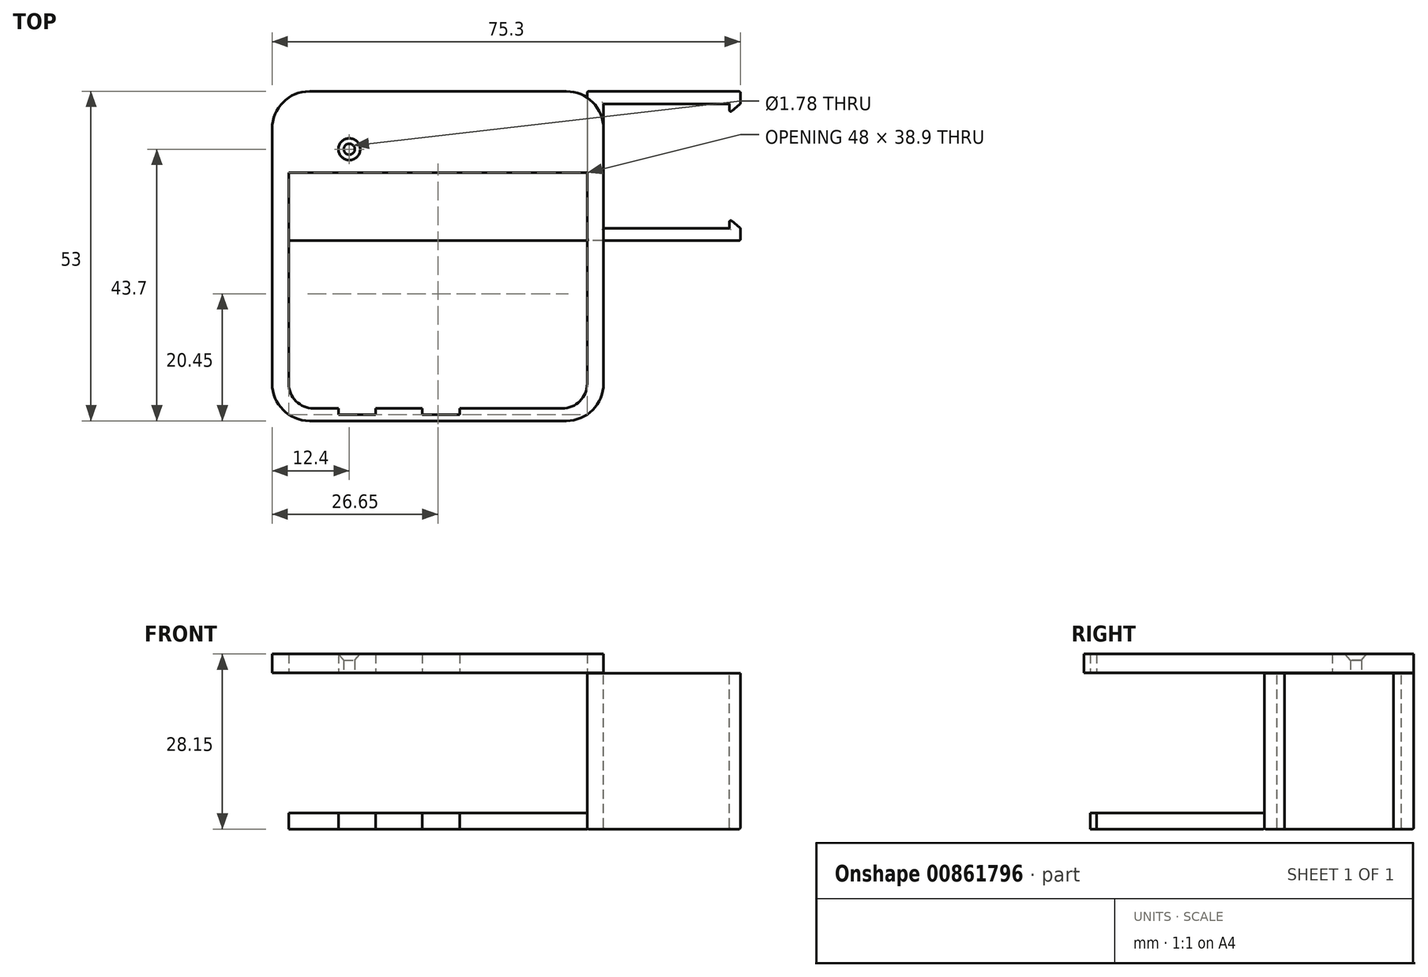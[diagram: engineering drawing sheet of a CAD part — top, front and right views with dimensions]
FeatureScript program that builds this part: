
annotation { "Feature Type Name" : "Feature", "Feature Type Description" : "" }
export const myFeature = defineFeature(function(context is Context, id is Id, definition is map)
    precondition{}
    {
        {
            var Q0;
            Q0=qCreatedBy(makeId("Top.planeOp"),FACE);
            var sketch = newSketch(context, id + "F0", { "sketchPlane" : qUnion([Q0])});
            skLineSegment(sketch, "E0.bottom", {"start": v(20.65, 26.5) * mm, "end": v(-20.65, 26.5) * mm});
            skLineSegment(sketch, "E0.top", {"start": v(20.65, -26.5) * mm, "end": v(-20.65, -26.5) * mm});
            skLineSegment(sketch, "E0.left", {"start": v(26.65, 20.5) * mm, "end": v(26.65, -20.5) * mm});
            skLineSegment(sketch, "E0.right", {"start": v(-26.65, 20.5) * mm, "end": v(-26.65, -20.5) * mm});
            skPoint(sketch, "E0.middle", {"position": v(0, 0) * mm});
            skPoint(sketch, "E1.visualSharp", {"position": v(-26.65, 26.5) * mm});
            skArc(sketch, "E1.filletArc", {"start": v(-20.65, 26.5) * mm, "mid": v(-24.9, 24.74) * mm, "end": v(-26.65, 20.5) * mm});
            skPoint(sketch, "E2.visualSharp", {"position": v(-26.65, -26.5) * mm});
            skArc(sketch, "E2.filletArc", {"start": v(-26.65, -20.5) * mm, "mid": v(-24.9, -24.74) * mm, "end": v(-20.65, -26.5) * mm});
            skPoint(sketch, "E3.visualSharp", {"position": v(26.65, -26.5) * mm});
            skArc(sketch, "E3.filletArc", {"start": v(20.65, -26.5) * mm, "mid": v(24.9, -24.74) * mm, "end": v(26.65, -20.5) * mm});
            skPoint(sketch, "E4.visualSharp", {"position": v(26.65, 26.5) * mm});
            skArc(sketch, "E4.filletArc", {"start": v(26.65, 20.5) * mm, "mid": v(24.9, 24.74) * mm, "end": v(20.65, 26.5) * mm});
            skSolve(sketch);
        }
        {
            var Q0;
            Q0=makeQuery(id+"F0.imprint","IMPRINT",FACE,{"disambiguationData":[TD([[makeQuery(id+"F0.imprint","IMPRINT",EDGE,{"derivedFrom":sQuery(id+"F0.wireOp",EDGE,"E0.bottom")}),1.0]])]});
            extrude(context, id + "F1", {"entities" : qUnion([Q0]), "depth" : (24.96 - 22.41) * mm, "offsetDistance" : 25 * mm});
        }
        {
            var Q0;
            Q0=makeQuery(id+"F1.opExtrude","CAP_FACE",FACE,{"disambiguationData":[OSD([sQuery(id+"F0.wireOp",EDGE,"E0.bottom"),sQuery(id+"F0.wireOp",EDGE,"E0.top"),sQuery(id+"F0.wireOp",EDGE,"E0.left"),sQuery(id+"F0.wireOp",EDGE,"E0.right"),sQuery(id+"F0.wireOp",EDGE,"E1.filletArc"),sQuery(id+"F0.wireOp",EDGE,"E2.filletArc"),sQuery(id+"F0.wireOp",EDGE,"E3.filletArc"),sQuery(id+"F0.wireOp",EDGE,"E4.filletArc")])],"isStart":false});
            var sketch = newSketch(context, id + "F2", { "sketchPlane" : qUnion([Q0])});
            skLineSegment(sketch, "E5.bottom", {"start": v(20, 24) * mm, "end": v(-20, 24) * mm});
            skLineSegment(sketch, "E5.top", {"start": v(20, -24) * mm, "end": v(-20, -24) * mm});
            skLineSegment(sketch, "E5.left", {"start": v(24, 20) * mm, "end": v(24, -20) * mm});
            skLineSegment(sketch, "E5.right", {"start": v(-24, 20) * mm, "end": v(-24, -20) * mm});
            skPoint(sketch, "E5.middle", {"position": v(0, 0) * mm});
            skPoint(sketch, "E6.visualSharp", {"position": v(-24, 24) * mm});
            skArc(sketch, "E6.filletArc", {"start": v(-20, 24) * mm, "mid": v(-22.83, 22.83) * mm, "end": v(-24, 20) * mm});
            skPoint(sketch, "E7.visualSharp", {"position": v(-24, -24) * mm});
            skArc(sketch, "E7.filletArc", {"start": v(-24, -20) * mm, "mid": v(-22.83, -22.83) * mm, "end": v(-20, -24) * mm});
            skPoint(sketch, "E8.visualSharp", {"position": v(24, -24) * mm});
            skArc(sketch, "E8.filletArc", {"start": v(20, -24) * mm, "mid": v(22.83, -22.83) * mm, "end": v(24, -20) * mm});
            skPoint(sketch, "E9.visualSharp", {"position": v(24, 24) * mm});
            skArc(sketch, "E9.filletArc", {"start": v(24, 20) * mm, "mid": v(22.83, 22.83) * mm, "end": v(20, 24) * mm});
            skSolve(sketch);
        }
        {
            var Q0;
            Q0=makeQuery(id+"F2.imprint","IMPRINT",FACE,{"disambiguationData":[TD([[makeQuery(id+"F2.imprint","IMPRINT",EDGE,{"derivedFrom":sQuery(id+"F2.wireOp",EDGE,"E5.bottom")}),-1.0]])]});
            extrude(context, id + "F3", {"entities" : qUnion([Q0]), "operationType" : NewBodyOperationType.ADD, "depth" : 22.5 * mm, "offsetDistance" : 25 * mm});
        }
        {
            var Q0;
            {var subQ0=sQuery(id+"F0.wireOp",EDGE,"E0.top");Q0=makeQuery(id+"F3.boolean.opBoolean","MERGE",FACE,{"derivedFrom":[makeQuery(id+"F1.opExtrude","SWEPT_FACE",FACE,{"disambiguationData":[OSD([subQ0])]}),makeQuery(id+"F3.opExtrude","SWEPT_FACE",FACE,{"disambiguationData":[OSD([subQ0])]})]});}
            var sketch = newSketch(context, id + "F4", { "sketchPlane" : qUnion([Q0])});
            skLineSegment(sketch, "E10.bottom", {"start": v(-15.5, 20.55) * mm, "end": v(-10.5, 20.55) * mm});
            skLineSegment(sketch, "E10.top", {"start": v(-15.5, 8.35) * mm, "end": v(-10.5, 8.35) * mm});
            skLineSegment(sketch, "E10.left", {"start": v(-15.5, 20.55) * mm, "end": v(-15.5, 8.35) * mm});
            skLineSegment(sketch, "E10.right", {"start": v(-10.5, 20.55) * mm, "end": v(-10.5, 8.35) * mm});
            skLineSegment(sketch, "E11.bottom", {"start": v(-2, 20.55) * mm, "end": v(3, 20.55) * mm});
            skLineSegment(sketch, "E11.top", {"start": v(-2, 8.35) * mm, "end": v(3, 8.35) * mm});
            skLineSegment(sketch, "E11.left", {"start": v(-2, 20.55) * mm, "end": v(-2, 8.35) * mm});
            skLineSegment(sketch, "E11.right", {"start": v(3, 20.55) * mm, "end": v(3, 8.35) * mm});
            skSolve(sketch);
        }
        {
            var Q0;
            Q0=makeQuery(id+"F4.imprint","IMPRINT",FACE,{"disambiguationData":[TD([[makeQuery(id+"F4.imprint","IMPRINT",EDGE,{"derivedFrom":sQuery(id+"F4.wireOp",EDGE,"E10.bottom")}),-1.0]])]});
            var Q1;
            Q1=makeQuery(id+"F4.imprint","IMPRINT",FACE,{"disambiguationData":[TD([[makeQuery(id+"F4.imprint","IMPRINT",EDGE,{"derivedFrom":sQuery(id+"F4.wireOp",EDGE,"E11.bottom")}),-1.0]])]});
            extrude(context, id + "F5", {"entities" : qUnion([Q0, Q1]), "operationType" : NewBodyOperationType.REMOVE, "oppositeDirection" : true, "depth" : 25 * mm, "offsetDistance" : 25 * mm});
        }
        {
            var Q0;
            Q0=makeQuery(id+"F1.opExtrude","CAP_FACE",FACE,{"disambiguationData":[OSD([sQuery(id+"F0.wireOp",EDGE,"E0.bottom"),sQuery(id+"F0.wireOp",EDGE,"E0.top"),sQuery(id+"F0.wireOp",EDGE,"E0.left"),sQuery(id+"F0.wireOp",EDGE,"E0.right"),sQuery(id+"F0.wireOp",EDGE,"E1.filletArc"),sQuery(id+"F0.wireOp",EDGE,"E2.filletArc"),sQuery(id+"F0.wireOp",EDGE,"E3.filletArc"),sQuery(id+"F0.wireOp",EDGE,"E4.filletArc")])],"isStart":false});
            var sketch = newSketch(context, id + "F6", { "sketchPlane" : qUnion([Q0])});
            skLineSegment(sketch, "E12.bottom", {"start": v(3, 24) * mm, "end": v(1.5, 24) * mm});
            skLineSegment(sketch, "E12.top", {"start": v(3, 11.7) * mm, "end": v(1.5, 11.7) * mm});
            skLineSegment(sketch, "E12.left", {"start": v(3, 24) * mm, "end": v(3, 11.7) * mm});
            skLineSegment(sketch, "E12.right", {"start": v(1.5, 24) * mm, "end": v(1.5, 11.7) * mm});
            skSolve(sketch);
        }
        {
            var Q0;
            Q0=makeQuery(id+"F6.imprint","IMPRINT",FACE,{"disambiguationData":[TD([[makeQuery(id+"F6.imprint","IMPRINT",EDGE,{"derivedFrom":sQuery(id+"F6.wireOp",EDGE,"E12.bottom")}),1.0]])]});
            var Q1;
            Q1=makeQuery(id+"F3.opExtrude","CAP_FACE",FACE,{"disambiguationData":[OSD([sQuery(id+"F0.wireOp",EDGE,"E0.bottom"),sQuery(id+"F0.wireOp",EDGE,"E0.top"),sQuery(id+"F0.wireOp",EDGE,"E0.left"),sQuery(id+"F0.wireOp",EDGE,"E0.right"),sQuery(id+"F0.wireOp",EDGE,"E1.filletArc"),sQuery(id+"F0.wireOp",EDGE,"E2.filletArc"),sQuery(id+"F0.wireOp",EDGE,"E3.filletArc"),sQuery(id+"F0.wireOp",EDGE,"E4.filletArc"),sQuery(id+"F2.wireOp",EDGE,"E5.bottom"),sQuery(id+"F2.wireOp",EDGE,"E5.top"),sQuery(id+"F2.wireOp",EDGE,"E5.left"),sQuery(id+"F2.wireOp",EDGE,"E5.right"),sQuery(id+"F2.wireOp",EDGE,"E6.filletArc"),sQuery(id+"F2.wireOp",EDGE,"E7.filletArc"),sQuery(id+"F2.wireOp",EDGE,"E8.filletArc"),sQuery(id+"F2.wireOp",EDGE,"E9.filletArc")])],"isStart":false});
            extrude(context, id + "F7", {"entities" : qUnion([Q0]), "operationType" : NewBodyOperationType.ADD, "endBound" : BoundingType.UP_TO_SURFACE, "depth" : 25 * mm, "endBoundEntityFace" : qUnion([Q1]), "offsetDistance" : 25 * mm});
        }
        {
            var Q0;
            Q0=makeQuery(id+"F7.opExtrude","CAP_EDGE",EDGE,{"disambiguationData":[OSD([sQuery(id+"F6.wireOp",EDGE,"E12.top")])],"isStart":false});
            chamfer(context, id + "F8", {"entities" : qUnion([Q0]), "chamferType" : ChamferType.TWO_OFFSETS, "width1" : 10 * mm, "oppositeDirection" : false, "width2" : 5 * mm, "tangentPropagation" : true});
        }
        {
            var Q0;
            {var subQ9=sQuery(id+"F2.wireOp",EDGE,"E9.filletArc");var subQ10=sQuery(id+"F2.wireOp",EDGE,"E5.bottom");Q0=makeQuery(id+"F7.boolean.opBoolean","SPLIT",FACE,{"disambiguationData":[TD([makeQuery(id+"F3.opExtrude","SWEPT_FACE",FACE,{"disambiguationData":[OSD([subQ9])]})])],"derivedFrom":makeQuery(id+"F3.opExtrude","SWEPT_FACE",FACE,{"disambiguationData":[OSD([subQ10])]})});}
            var sketch = newSketch(context, id + "F9", { "sketchPlane" : qUnion([Q0])});
            skLineSegment(sketch, "E13.bottom", {"start": v(14, 2.55) * mm, "end": v(4, 2.55) * mm});
            skLineSegment(sketch, "E13.top", {"start": v(14, 9.55) * mm, "end": v(4, 9.55) * mm});
            skLineSegment(sketch, "E13.left", {"start": v(14, 2.55) * mm, "end": v(14, 9.55) * mm});
            skLineSegment(sketch, "E13.right", {"start": v(4, 2.55) * mm, "end": v(4, 9.55) * mm});
            skSolve(sketch);
        }
        {
            var Q0;
            Q0=makeQuery(id+"F9.imprint","IMPRINT",FACE,{"disambiguationData":[TD([[makeQuery(id+"F9.imprint","IMPRINT",EDGE,{"derivedFrom":sQuery(id+"F9.wireOp",EDGE,"E13.bottom")}),-1.0]])]});
            extrude(context, id + "F10", {"entities" : qUnion([Q0]), "operationType" : NewBodyOperationType.REMOVE, "oppositeDirection" : true, "depth" : 25 * mm, "offsetDistance" : 25 * mm});
        }
        {
            var Q0;
            Q0=makeQuery(id+"F3.opExtrude","SWEPT_FACE",FACE,{"disambiguationData":[OSD([sQuery(id+"F2.wireOp",EDGE,"E5.top")])]});
            var sketch = newSketch(context, id + "F11", { "sketchPlane" : qUnion([Q0])});
            skLineSegment(sketch, "E14.bottom", {"start": v(-3, 20.55) * mm, "end": v(2, 20.55) * mm});
            skLineSegment(sketch, "E14.top", {"start": v(-3, 25.05) * mm, "end": v(2, 25.05) * mm});
            skLineSegment(sketch, "E14.left", {"start": v(-3, 20.55) * mm, "end": v(-3, 25.05) * mm});
            skLineSegment(sketch, "E14.right", {"start": v(2, 20.55) * mm, "end": v(2, 25.05) * mm});
            skLineSegment(sketch, "E15.bottom", {"start": v(10.5, 20.55) * mm, "end": v(15.5, 20.55) * mm});
            skLineSegment(sketch, "E15.top", {"start": v(10.5, 25.05) * mm, "end": v(15.5, 25.05) * mm});
            skLineSegment(sketch, "E15.left", {"start": v(10.5, 20.55) * mm, "end": v(10.5, 25.05) * mm});
            skLineSegment(sketch, "E15.right", {"start": v(15.5, 20.55) * mm, "end": v(15.5, 25.05) * mm});
            skSolve(sketch);
        }
        {
            var Q0;
            Q0=makeQuery(id+"F11.imprint","IMPRINT",FACE,{"disambiguationData":[TD([[makeQuery(id+"F11.imprint","IMPRINT",EDGE,{"derivedFrom":sQuery(id+"F11.wireOp",EDGE,"E14.bottom")}),-1.0]])]});
            var Q1;
            Q1=makeQuery(id+"F11.imprint","IMPRINT",FACE,{"disambiguationData":[TD([[makeQuery(id+"F11.imprint","IMPRINT",EDGE,{"derivedFrom":sQuery(id+"F11.wireOp",EDGE,"E15.bottom")}),-1.0]])]});
            extrude(context, id + "F12", {"entities" : qUnion([Q0, Q1]), "operationType" : NewBodyOperationType.REMOVE, "oppositeDirection" : true, "depth" : 1.5 * mm, "offsetDistance" : 25 * mm});
        }
        {
            var Q0;
            Q0=makeQuery(id+"F10.boolean.opBoolean","MERGE",FACE,{"derivedFrom":[makeQuery(id+"F1.opExtrude","CAP_FACE",FACE,{"disambiguationData":[OSD([sQuery(id+"F0.wireOp",EDGE,"E0.bottom"),sQuery(id+"F0.wireOp",EDGE,"E0.top"),sQuery(id+"F0.wireOp",EDGE,"E0.left"),sQuery(id+"F0.wireOp",EDGE,"E0.right"),sQuery(id+"F0.wireOp",EDGE,"E1.filletArc"),sQuery(id+"F0.wireOp",EDGE,"E2.filletArc"),sQuery(id+"F0.wireOp",EDGE,"E3.filletArc"),sQuery(id+"F0.wireOp",EDGE,"E4.filletArc")])],"isStart":false}),makeQuery(id+"F10.opExtrude","SWEPT_FACE",FACE,{"disambiguationData":[OSD([sQuery(id+"F9.wireOp",EDGE,"E13.bottom")])]})]});
            var sketch = newSketch(context, id + "F13", { "sketchPlane" : qUnion([Q0])});
            skCircle(sketch, "E16", {"center": v(-14.25, 17.2) * mm, "radius": 4.5 * mm});
            skSolve(sketch);
        }
        {
            var Q0;
            Q0=makeQuery(id+"F13.imprint","IMPRINT",FACE,{"disambiguationData":[TD([[makeQuery(id+"F13.imprint","IMPRINT",EDGE,{"derivedFrom":sQuery(id+"F13.wireOp",EDGE,"E16")}),1.0]])]});
            var Q1;
            Q1=makeQuery(id+"F7.boolean.opBoolean","MERGE",FACE,{"derivedFrom":[makeQuery(id+"F3.opExtrude","CAP_FACE",FACE,{"disambiguationData":[OSD([sQuery(id+"F0.wireOp",EDGE,"E0.bottom"),sQuery(id+"F0.wireOp",EDGE,"E0.top"),sQuery(id+"F0.wireOp",EDGE,"E0.left"),sQuery(id+"F0.wireOp",EDGE,"E0.right"),sQuery(id+"F0.wireOp",EDGE,"E1.filletArc"),sQuery(id+"F0.wireOp",EDGE,"E2.filletArc"),sQuery(id+"F0.wireOp",EDGE,"E3.filletArc"),sQuery(id+"F0.wireOp",EDGE,"E4.filletArc"),sQuery(id+"F2.wireOp",EDGE,"E5.bottom"),sQuery(id+"F2.wireOp",EDGE,"E5.top"),sQuery(id+"F2.wireOp",EDGE,"E5.left"),sQuery(id+"F2.wireOp",EDGE,"E5.right"),sQuery(id+"F2.wireOp",EDGE,"E6.filletArc"),sQuery(id+"F2.wireOp",EDGE,"E7.filletArc"),sQuery(id+"F2.wireOp",EDGE,"E8.filletArc"),sQuery(id+"F2.wireOp",EDGE,"E9.filletArc")])],"isStart":false}),makeQuery(id+"F7.opExtrude","CAP_FACE",FACE,{"disambiguationData":[OSD([sQuery(id+"F6.wireOp",EDGE,"E12.bottom"),sQuery(id+"F6.wireOp",EDGE,"E12.top"),sQuery(id+"F6.wireOp",EDGE,"E12.left"),sQuery(id+"F6.wireOp",EDGE,"E12.right")])],"isStart":false})]});
            extrude(context, id + "F14", {"entities" : qUnion([Q0]), "operationType" : NewBodyOperationType.ADD, "endBound" : BoundingType.UP_TO_SURFACE, "depth" : 25 * mm, "endBoundEntityFace" : qUnion([Q1]), "offsetDistance" : 25 * mm});
        }
        {
            var Q0;
            Q0=makeQuery(id+"F7.boolean.opBoolean","MERGE",FACE,{"derivedFrom":[makeQuery(id+"F3.opExtrude","CAP_FACE",FACE,{"disambiguationData":[OSD([sQuery(id+"F0.wireOp",EDGE,"E0.bottom"),sQuery(id+"F0.wireOp",EDGE,"E0.top"),sQuery(id+"F0.wireOp",EDGE,"E0.left"),sQuery(id+"F0.wireOp",EDGE,"E0.right"),sQuery(id+"F0.wireOp",EDGE,"E1.filletArc"),sQuery(id+"F0.wireOp",EDGE,"E2.filletArc"),sQuery(id+"F0.wireOp",EDGE,"E3.filletArc"),sQuery(id+"F0.wireOp",EDGE,"E4.filletArc"),sQuery(id+"F2.wireOp",EDGE,"E5.bottom"),sQuery(id+"F2.wireOp",EDGE,"E5.top"),sQuery(id+"F2.wireOp",EDGE,"E5.left"),sQuery(id+"F2.wireOp",EDGE,"E5.right"),sQuery(id+"F2.wireOp",EDGE,"E6.filletArc"),sQuery(id+"F2.wireOp",EDGE,"E7.filletArc"),sQuery(id+"F2.wireOp",EDGE,"E8.filletArc"),sQuery(id+"F2.wireOp",EDGE,"E9.filletArc")])],"isStart":false}),makeQuery(id+"F7.opExtrude","CAP_FACE",FACE,{"disambiguationData":[OSD([sQuery(id+"F6.wireOp",EDGE,"E12.bottom"),sQuery(id+"F6.wireOp",EDGE,"E12.top"),sQuery(id+"F6.wireOp",EDGE,"E12.left"),sQuery(id+"F6.wireOp",EDGE,"E12.right")])],"isStart":false})]});
            cPlane(context, id + "F15", {"entities" : qUnion([Q0]), "cplaneType" : CPlaneType.OFFSET, "offset" : .1 * mm, "width" : 150 * mm, "height" : 150 * mm});
        }
        {
            var Q0;
            Q0=qCreatedBy(id+"F15.planeOp",FACE);
            var sketch = newSketch(context, id + "F16", { "sketchPlane" : qUnion([Q0])});
            skLineSegment(sketch, "E17.0", {"start": v(20.65, 26.5) * mm, "end": v(-20.65, 26.5) * mm});
            skArc(sketch, "E18.0", {"start": v(-20.65, 26.5) * mm, "mid": v(-24.9, 24.74) * mm, "end": v(-26.65, 20.5) * mm});
            skLineSegment(sketch, "E19.0", {"start": v(-26.65, 20.5) * mm, "end": v(-26.65, -20.5) * mm});
            skArc(sketch, "E20.0", {"start": v(-26.65, -20.5) * mm, "mid": v(-24.9, -24.74) * mm, "end": v(-20.65, -26.5) * mm});
            skLineSegment(sketch, "E21.0", {"start": v(20.65, -26.5) * mm, "end": v(-20.65, -26.5) * mm});
            skArc(sketch, "E22.0", {"start": v(20.65, -26.5) * mm, "mid": v(24.9, -24.74) * mm, "end": v(26.65, -20.5) * mm});
            skLineSegment(sketch, "E23.0", {"start": v(26.65, 20.5) * mm, "end": v(26.65, -20.5) * mm});
            skArc(sketch, "E24.0", {"start": v(26.65, 20.5) * mm, "mid": v(24.9, 24.74) * mm, "end": v(20.65, 26.5) * mm});
            skSolve(sketch);
        }
        {
            var Q0;
            Q0=makeQuery(id+"F16.imprint","IMPRINT",FACE,{"disambiguationData":[TD([[makeQuery(id+"F16.imprint","IMPRINT",EDGE,{"derivedFrom":sQuery(id+"F16.wireOp",EDGE,"E17.0")}),1.0]])]});
            extrude(context, id + "F17", {"entities" : qUnion([Q0]), "depth" : 3 * mm, "offsetDistance" : 25 * mm});
        }
        {
            var Q0;
            Q0=makeQuery(id+"F17.opExtrude","CAP_FACE",FACE,{"disambiguationData":[OSD([sQuery(id+"F16.wireOp",EDGE,"E17.0"),sQuery(id+"F16.wireOp",EDGE,"E18.0"),sQuery(id+"F16.wireOp",EDGE,"E19.0"),sQuery(id+"F16.wireOp",EDGE,"E20.0"),sQuery(id+"F16.wireOp",EDGE,"E21.0"),sQuery(id+"F16.wireOp",EDGE,"E22.0"),sQuery(id+"F16.wireOp",EDGE,"E23.0"),sQuery(id+"F16.wireOp",EDGE,"E24.0")])],"isStart":false});
            var sketch = newSketch(context, id + "F18", { "sketchPlane" : qUnion([Q0])});
            skPoint(sketch, "E25", {"position": v(-14.25, 17.2) * mm});
            skSolve(sketch);
        }
        {
            var Q0;
            Q0=sQuery(id+"F18.wireOp",VERTEX,"E25");
            var Q1;
            Q1=makeQuery(id+"F1.opExtrude","SWEPT_BODY",BODY,{"disambiguationData":[OSD([sQuery(id+"F0.wireOp",EDGE,"E0.bottom"),sQuery(id+"F0.wireOp",EDGE,"E0.top"),sQuery(id+"F0.wireOp",EDGE,"E0.left"),sQuery(id+"F0.wireOp",EDGE,"E0.right"),sQuery(id+"F0.wireOp",EDGE,"E1.filletArc"),sQuery(id+"F0.wireOp",EDGE,"E2.filletArc"),sQuery(id+"F0.wireOp",EDGE,"E3.filletArc"),sQuery(id+"F0.wireOp",EDGE,"E4.filletArc")])]});
            var Q2;
            Q2=makeQuery(id+"F17.opExtrude","SWEPT_BODY",BODY,{"disambiguationData":[OSD([sQuery(id+"F16.wireOp",EDGE,"E17.0"),sQuery(id+"F16.wireOp",EDGE,"E18.0"),sQuery(id+"F16.wireOp",EDGE,"E19.0"),sQuery(id+"F16.wireOp",EDGE,"E20.0"),sQuery(id+"F16.wireOp",EDGE,"E21.0"),sQuery(id+"F16.wireOp",EDGE,"E22.0"),sQuery(id+"F16.wireOp",EDGE,"E23.0"),sQuery(id+"F16.wireOp",EDGE,"E24.0")])]});
            hole(context, id + "F19", {"style" : HoleStyle.C_SINK, "endStyle" : HoleEndStyle.BLIND, "standardTappedOrClearance" : lookupTablePath({ "fit" : "Normal (ASME)", "standard" : "ANSI", "size" : "#0", "type" : "Clearance" }), "standardBlindInLast" : lookupTablePath({ "fit" : "Free", "standard" : "ANSI", "size" : "#0", "type" : "Clearance" }), "holeDiameter" : 1.78 * mm, "cSinkDiameter" : 3.5 * mm, "cSinkAngle" : 82 * degree, "majorDiameter" : 5 * mm, "holeDepth" : 12 * mm, "isTappedThrough" : true, "tappedDepth" : 12 * mm, "tapClearance" : 3, "locations" : qUnion([Q0]), "scope" : qUnion([Q1, Q2]), "startStyle" : HoleStartStyle.PART});
        }
        {
            var Q0;
            {var subQ0=sQuery(id+"F0.wireOp",EDGE,"E0.left");Q0=makeQuery(id+"F3.boolean.opBoolean","MERGE",FACE,{"derivedFrom":[makeQuery(id+"F1.opExtrude","SWEPT_FACE",FACE,{"disambiguationData":[OSD([subQ0])]}),makeQuery(id+"F3.opExtrude","SWEPT_FACE",FACE,{"disambiguationData":[OSD([subQ0])]})]});}
            var sketch = newSketch(context, id + "F20", { "sketchPlane" : qUnion([Q0])});
            skLineSegment(sketch, "E26.bottom", {"start": v(4.5, 0) * mm, "end": v(2.5, 0) * mm});
            skLineSegment(sketch, "E26.top", {"start": v(4.5, 25.15) * mm, "end": v(2.5, 25.15) * mm});
            skLineSegment(sketch, "E26.left", {"start": v(4.5, 0) * mm, "end": v(4.5, 25.15) * mm});
            skLineSegment(sketch, "E26.right", {"start": v(2.5, 0) * mm, "end": v(2.5, 25.15) * mm});
            skLineSegment(sketch, "E27.bottom", {"start": v(26.5, 0) * mm, "end": v(24.5, 0) * mm});
            skLineSegment(sketch, "E27.top", {"start": v(26.5, 25.05) * mm, "end": v(24.5, 25.05) * mm});
            skLineSegment(sketch, "E27.left", {"start": v(26.5, 0) * mm, "end": v(26.5, 25.05) * mm});
            skLineSegment(sketch, "E27.right", {"start": v(24.5, 0) * mm, "end": v(24.5, 25.05) * mm});
            skSolve(sketch);
        }
        {
            var Q0;
            {var subQ0=sQuery(id+"F20.wireOp",EDGE,"E26.bottom");Q0=makeQuery(id+"F20.imprint","IMPRINT",FACE,{"disambiguationData":[TD([[makeQuery(id+"F20.imprint","IMPRINT",EDGE,{"derivedFrom":subQ0}),-1.0]])]});}
            var Q1;
            Q1=makeQuery(id+"F20.imprint","IMPRINT",FACE,{"disambiguationData":[TD([[makeQuery(id+"F20.imprint","IMPRINT",EDGE,{"derivedFrom":sQuery(id+"F20.wireOp",EDGE,"E27.bottom")}),-1.0]])]});
            var Q2;
            {var subQ0=sQuery(id+"F0.wireOp",EDGE,"E4.filletArc");Q2=makeQuery(id+"F3.boolean.opBoolean","MERGE",FACE,{"derivedFrom":[makeQuery(id+"F1.opExtrude","SWEPT_FACE",FACE,{"disambiguationData":[OSD([subQ0])]}),makeQuery(id+"F3.opExtrude","SWEPT_FACE",FACE,{"disambiguationData":[OSD([subQ0])]})]});}
            var Q3;
            Q3=makeQuery(id+"F1.opExtrude","SWEPT_BODY",BODY,{"disambiguationData":[OSD([sQuery(id+"F0.wireOp",EDGE,"E0.bottom"),sQuery(id+"F0.wireOp",EDGE,"E0.top"),sQuery(id+"F0.wireOp",EDGE,"E0.left"),sQuery(id+"F0.wireOp",EDGE,"E0.right"),sQuery(id+"F0.wireOp",EDGE,"E1.filletArc"),sQuery(id+"F0.wireOp",EDGE,"E2.filletArc"),sQuery(id+"F0.wireOp",EDGE,"E3.filletArc"),sQuery(id+"F0.wireOp",EDGE,"E4.filletArc")])]});
            extrude(context, id + "F21", {"entities" : qUnion([Q0, Q1]), "operationType" : NewBodyOperationType.ADD, "depth" : 22 * mm, "offsetDistance" : 25 * mm});
        }
        {
            var Q0;
            Q0=makeQuery(id+"F21.opExtrude","CAP_FACE",FACE,{"disambiguationData":[OSD([sQuery(id+"F20.wireOp",EDGE,"E27.bottom"),sQuery(id+"F20.wireOp",EDGE,"E27.top"),sQuery(id+"F20.wireOp",EDGE,"E27.left"),sQuery(id+"F20.wireOp",EDGE,"E27.right")])],"isStart":true});
            var sketch = newSketch(context, id + "F22", { "sketchPlane" : qUnion([Q0])});
            skLineSegment(sketch, "E28.0.0", {"start": v(-26.5, 25.05) * mm, "end": v(-26.5, 0) * mm});
            skLineSegment(sketch, "E28.0.1", {"start": v(-26.5, 0) * mm, "end": v(-24.5, 0) * mm});
            skLineSegment(sketch, "E28.0.2", {"start": v(-24.5, 0) * mm, "end": v(-24.5, 25.05) * mm});
            skLineSegment(sketch, "E28.0.3", {"start": v(-24.5, 25.05) * mm, "end": v(-26.5, 25.05) * mm});
            skSolve(sketch);
        }
        {
            var Q0;
            Q0=makeQuery(id+"F22.imprint","IMPRINT",FACE,{"disambiguationData":[TD([[makeQuery(id+"F22.imprint","IMPRINT",EDGE,{"derivedFrom":sQuery(id+"F22.wireOp",EDGE,"E28.0.0")}),-1.0]])]});
            extrude(context, id + "F23", {"entities" : qUnion([Q0]), "operationType" : NewBodyOperationType.ADD, "endBound" : BoundingType.UP_TO_NEXT, "depth" : 25 * mm, "offsetDistance" : 25 * mm});
        }
        {
            var Q0;
            {var subQ0=sQuery(id+"F0.wireOp",EDGE,"E0.left");Q0=makeQuery(id+"F23.boolean.opBoolean","MERGE",FACE,{"derivedFrom":[makeQuery(id+"F21.opExtrude","SWEPT_FACE",FACE,{"disambiguationData":[OSD([sQuery(id+"F20.wireOp",EDGE,"E27.top")])]}),makeQuery(id+"F21.boolean.opBoolean","MERGE",FACE,{"derivedFrom":[makeQuery(id+"F7.boolean.opBoolean","MERGE",FACE,{"derivedFrom":[makeQuery(id+"F3.opExtrude","CAP_FACE",FACE,{"disambiguationData":[OSD([sQuery(id+"F0.wireOp",EDGE,"E0.bottom"),sQuery(id+"F0.wireOp",EDGE,"E0.top"),subQ0,sQuery(id+"F0.wireOp",EDGE,"E0.right"),sQuery(id+"F0.wireOp",EDGE,"E1.filletArc"),sQuery(id+"F0.wireOp",EDGE,"E2.filletArc"),sQuery(id+"F0.wireOp",EDGE,"E3.filletArc"),sQuery(id+"F0.wireOp",EDGE,"E4.filletArc"),sQuery(id+"F2.wireOp",EDGE,"E5.bottom"),sQuery(id+"F2.wireOp",EDGE,"E5.top"),sQuery(id+"F2.wireOp",EDGE,"E5.left"),sQuery(id+"F2.wireOp",EDGE,"E5.right"),sQuery(id+"F2.wireOp",EDGE,"E6.filletArc"),sQuery(id+"F2.wireOp",EDGE,"E7.filletArc"),sQuery(id+"F2.wireOp",EDGE,"E8.filletArc"),sQuery(id+"F2.wireOp",EDGE,"E9.filletArc")])],"isStart":false}),makeQuery(id+"F7.opExtrude","CAP_FACE",FACE,{"disambiguationData":[OSD([sQuery(id+"F6.wireOp",EDGE,"E12.bottom"),sQuery(id+"F6.wireOp",EDGE,"E12.top"),sQuery(id+"F6.wireOp",EDGE,"E12.left"),sQuery(id+"F6.wireOp",EDGE,"E12.right")])],"isStart":false})]}),makeQuery(id+"F21.opExtrude","SWEPT_FACE",FACE,{"disambiguationData":[OSD([subQ0])]})]}),makeQuery(id+"F23.opExtrude","SWEPT_FACE",FACE,{"disambiguationData":[OSD([sQuery(id+"F22.wireOp",EDGE,"E28.0.3")])]})]});}
            var sketch = newSketch(context, id + "F24", { "sketchPlane" : qUnion([Q0])});
            skLineSegment(sketch, "E29", {"start": v(48.65, 24.5) * mm, "end": v(46.85, 23) * mm});
            skLineSegment(sketch, "E30", {"start": v(46.85, 23) * mm, "end": v(46.85, 24.5) * mm});
            skLineSegment(sketch, "E31", {"start": v(48.65, 4.5) * mm, "end": v(46.85, 6) * mm});
            skLineSegment(sketch, "E32", {"start": v(46.85, 6) * mm, "end": v(46.85, 4.5) * mm});
            skSolve(sketch);
        }
        {
            var Q0;
            {var subQ0=sQuery(id+"F24.wireOp",EDGE,"E29");Q0=makeQuery(id+"F24.imprint","IMPRINT",FACE,{"disambiguationData":[TD([[makeQuery(id+"F24.imprint","IMPRINT",EDGE,{"derivedFrom":subQ0}),-1.0]])]});}
            var Q1;
            {var subQ0=sQuery(id+"F24.wireOp",EDGE,"E31");Q1=makeQuery(id+"F24.imprint","IMPRINT",FACE,{"disambiguationData":[TD([[makeQuery(id+"F24.imprint","IMPRINT",EDGE,{"derivedFrom":subQ0}),1.0]])]});}
            var Q2;
            Q2=makeQuery(id+"F23.boolean.opBoolean","MERGE",FACE,{"derivedFrom":[makeQuery(id+"F21.opExtrude","SWEPT_FACE",FACE,{"disambiguationData":[OSD([sQuery(id+"F20.wireOp",EDGE,"E27.bottom")])]}),makeQuery(id+"F21.boolean.opBoolean","MERGE",FACE,{"derivedFrom":[makeQuery(id+"F1.opExtrude","CAP_FACE",FACE,{"disambiguationData":[OSD([sQuery(id+"F0.wireOp",EDGE,"E0.bottom"),sQuery(id+"F0.wireOp",EDGE,"E0.top"),sQuery(id+"F0.wireOp",EDGE,"E0.left"),sQuery(id+"F0.wireOp",EDGE,"E0.right"),sQuery(id+"F0.wireOp",EDGE,"E1.filletArc"),sQuery(id+"F0.wireOp",EDGE,"E2.filletArc"),sQuery(id+"F0.wireOp",EDGE,"E3.filletArc"),sQuery(id+"F0.wireOp",EDGE,"E4.filletArc")])],"isStart":true}),makeQuery(id+"F21.opExtrude","SWEPT_FACE",FACE,{"disambiguationData":[OSD([sQuery(id+"F20.wireOp",EDGE,"E26.bottom")])]})]}),makeQuery(id+"F23.opExtrude","SWEPT_FACE",FACE,{"disambiguationData":[OSD([sQuery(id+"F22.wireOp",EDGE,"E28.0.1")])]})]});
            extrude(context, id + "F25", {"entities" : qUnion([Q0, Q1]), "operationType" : NewBodyOperationType.ADD, "endBound" : BoundingType.UP_TO_SURFACE, "oppositeDirection" : true, "depth" : 25 * mm, "endBoundEntityFace" : qUnion([Q2]), "offsetDistance" : 25 * mm});
        }
        {
            var Q0;
            Q0=makeQuery(id+"F25.opExtrude","SWEPT_EDGE",EDGE,{"disambiguationData":[OSD([sQuery(id+"F24.wireOp",EDGE,"E29"),sQuery(id+"F24.wireOp",EDGE,"E30")])]});
            var Q1;
            Q1=makeQuery(id+"F25.opExtrude","SWEPT_EDGE",EDGE,{"disambiguationData":[OSD([sQuery(id+"F24.wireOp",EDGE,"E31"),sQuery(id+"F24.wireOp",EDGE,"E32")])]});
            fillet(context, id + "F26", {"entities" : qUnion([Q0, Q1]), "radius" : .25 * mm, "tangentPropagation" : true, "allowEdgeOverflow" : false});
        }
        {
            var Q0;
            Q0=makeQuery(id+"F21.opExtrude","CAP_EDGE",EDGE,{"disambiguationData":[OSD([sQuery(id+"F20.wireOp",EDGE,"E27.left")])],"isStart":false});
            var Q1;
            Q1=makeQuery(id+"F21.opExtrude","CAP_EDGE",EDGE,{"disambiguationData":[OSD([sQuery(id+"F20.wireOp",EDGE,"E26.right")])],"isStart":false});
            var Q2;
            Q2=makeQuery(id+"F21.opExtrude","SWEPT_EDGE",EDGE,{"disambiguationData":[OSD([sQuery(id+"F0.wireOp",EDGE,"E0.left"),sQuery(id+"F20.wireOp",EDGE,"E26.bottom"),sQuery(id+"F20.wireOp",EDGE,"E26.right")])]});
            var Q3;
            Q3=makeQuery(id+"F23.boolean.opBoolean","MERGE",EDGE,{"derivedFrom":[makeQuery(id+"F1.opExtrude","CAP_EDGE",EDGE,{"disambiguationData":[OSD([sQuery(id+"F0.wireOp",EDGE,"E0.bottom")])],"isStart":true}),makeQuery(id+"F21.opExtrude","SWEPT_EDGE",EDGE,{"disambiguationData":[OSD([sQuery(id+"F20.wireOp",EDGE,"E27.bottom"),sQuery(id+"F20.wireOp",EDGE,"E27.left")])]}),makeQuery(id+"F23.opExtrude","SWEPT_EDGE",EDGE,{"disambiguationData":[OSD([sQuery(id+"F22.wireOp",EDGE,"E28.0.0"),sQuery(id+"F22.wireOp",EDGE,"E28.0.1")])]})]});
            var Q4;
            Q4=makeQuery(id+"F21.opExtrude","CAP_EDGE",EDGE,{"disambiguationData":[OSD([sQuery(id+"F20.wireOp",EDGE,"E27.bottom")])],"isStart":false});
            var Q5;
            Q5=makeQuery(id+"F21.opExtrude","CAP_EDGE",EDGE,{"disambiguationData":[OSD([sQuery(id+"F20.wireOp",EDGE,"E26.bottom")])],"isStart":false});
            var Q6;
            {var subQ0=sQuery(id+"F20.wireOp",EDGE,"E26.left");Q6=makeQuery(id+"F25.boolean.opBoolean","MERGE",EDGE,{"derivedFrom":[makeQuery(id+"F21.opExtrude","CAP_EDGE",EDGE,{"disambiguationData":[OSD([subQ0])],"isStart":false}),makeQuery(id+"F25.opExtrude","SWEPT_EDGE",EDGE,{"disambiguationData":[OSD([sQuery(id+"F0.wireOp",EDGE,"E0.left"),subQ0,sQuery(id+"F24.wireOp",EDGE,"E31")])]})]});}
            var Q7;
            {var subQ0=sQuery(id+"F20.wireOp",EDGE,"E27.right");Q7=makeQuery(id+"F25.boolean.opBoolean","MERGE",EDGE,{"derivedFrom":[makeQuery(id+"F21.opExtrude","CAP_EDGE",EDGE,{"disambiguationData":[OSD([subQ0])],"isStart":false}),makeQuery(id+"F25.opExtrude","SWEPT_EDGE",EDGE,{"disambiguationData":[OSD([sQuery(id+"F20.wireOp",EDGE,"E27.top"),subQ0,sQuery(id+"F22.wireOp",EDGE,"E28.0.2"),sQuery(id+"F22.wireOp",EDGE,"E28.0.3"),sQuery(id+"F24.wireOp",EDGE,"E29")])]})]});}
            var Q8;
            Q8=makeQuery(id+"F25.opExtrude","CAP_EDGE",EDGE,{"disambiguationData":[OSD([sQuery(id+"F24.wireOp",EDGE,"E29")])],"isStart":false});
            var Q9;
            Q9=makeQuery(id+"F25.opExtrude","CAP_EDGE",EDGE,{"disambiguationData":[OSD([sQuery(id+"F24.wireOp",EDGE,"E31")])],"isStart":false});
            fillet(context, id + "F27", {"entities" : qUnion([Q0, Q1, Q2, Q3, Q4, Q5, Q6, Q7, Q8, Q9]), "radius" : .25 * mm, "tangentPropagation" : true, "defaultsChanged" : false, "vertexSettings" : [], "allowEdgeOverflow" : false});
        }
        {
            var Q0;
            Q0=makeQuery(id+"F10.boolean.opBoolean","COPY",EDGE,{"derivedFrom":makeQuery(id+"F10.opExtrude","CAP_EDGE",EDGE,{"disambiguationData":[OSD([sQuery(id+"F9.wireOp",EDGE,"E13.left")])],"isStart":true})});
            var Q1;
            {var subQ0=sQuery(id+"F0.wireOp",EDGE,"E0.bottom");Q1=makeQuery(id+"F10.boolean.opBoolean","INTERSECT",EDGE,{"derivedFrom":[makeQuery(id+"F3.boolean.opBoolean","MERGE",FACE,{"derivedFrom":[makeQuery(id+"F1.opExtrude","SWEPT_FACE",FACE,{"disambiguationData":[OSD([subQ0])]}),makeQuery(id+"F3.opExtrude","SWEPT_FACE",FACE,{"disambiguationData":[OSD([subQ0])]})]}),makeQuery(id+"F10.opExtrude","SWEPT_FACE",FACE,{"disambiguationData":[OSD([sQuery(id+"F9.wireOp",EDGE,"E13.left")])]})]});}
            var Q2;
            {var subQ0=sQuery(id+"F0.wireOp",EDGE,"E0.bottom");Q2=makeQuery(id+"F10.boolean.opBoolean","INTERSECT",EDGE,{"derivedFrom":[makeQuery(id+"F3.boolean.opBoolean","MERGE",FACE,{"derivedFrom":[makeQuery(id+"F1.opExtrude","SWEPT_FACE",FACE,{"disambiguationData":[OSD([subQ0])]}),makeQuery(id+"F3.opExtrude","SWEPT_FACE",FACE,{"disambiguationData":[OSD([subQ0])]})]}),makeQuery(id+"F10.opExtrude","SWEPT_FACE",FACE,{"disambiguationData":[OSD([sQuery(id+"F9.wireOp",EDGE,"E13.bottom")])]})]});}
            var Q3;
            {var subQ0=sQuery(id+"F0.wireOp",EDGE,"E0.bottom");Q3=makeQuery(id+"F10.boolean.opBoolean","INTERSECT",EDGE,{"derivedFrom":[makeQuery(id+"F3.boolean.opBoolean","MERGE",FACE,{"derivedFrom":[makeQuery(id+"F1.opExtrude","SWEPT_FACE",FACE,{"disambiguationData":[OSD([subQ0])]}),makeQuery(id+"F3.opExtrude","SWEPT_FACE",FACE,{"disambiguationData":[OSD([subQ0])]})]}),makeQuery(id+"F10.opExtrude","SWEPT_FACE",FACE,{"disambiguationData":[OSD([sQuery(id+"F9.wireOp",EDGE,"E13.right")])]})]});}
            var Q4;
            Q4=makeQuery(id+"F10.boolean.opBoolean","COPY",EDGE,{"derivedFrom":makeQuery(id+"F10.opExtrude","CAP_EDGE",EDGE,{"disambiguationData":[OSD([sQuery(id+"F9.wireOp",EDGE,"E13.right")])],"isStart":true})});
            fillet(context, id + "F28", {"entities" : qUnion([Q0, Q1, Q2, Q3, Q4]), "radius" : .25 * mm, "tangentPropagation" : true, "allowEdgeOverflow" : false});
        }
        {
            var Q0;
            Q0=makeQuery(id+"F5.boolean.opBoolean","COPY",EDGE,{"derivedFrom":makeQuery(id+"F5.opExtrude","CAP_EDGE",EDGE,{"disambiguationData":[OSD([sQuery(id+"F4.wireOp",EDGE,"E11.left")])],"isStart":true})});
            var Q1;
            Q1=makeQuery(id+"F12.boolean.opBoolean","MERGE",EDGE,{"derivedFrom":[makeQuery(id+"F5.boolean.opBoolean","INTERSECT",EDGE,{"derivedFrom":[makeQuery(id+"F3.opExtrude","SWEPT_FACE",FACE,{"disambiguationData":[OSD([sQuery(id+"F2.wireOp",EDGE,"E5.top")])]}),makeQuery(id+"F5.opExtrude","SWEPT_FACE",FACE,{"disambiguationData":[OSD([sQuery(id+"F4.wireOp",EDGE,"E11.left")])]})]}),makeQuery(id+"F12.opExtrude","CAP_EDGE",EDGE,{"disambiguationData":[OSD([sQuery(id+"F11.wireOp",EDGE,"E14.right")])],"isStart":true})]});
            var Q2;
            Q2=makeQuery(id+"F5.boolean.opBoolean","COPY",EDGE,{"derivedFrom":makeQuery(id+"F5.opExtrude","CAP_EDGE",EDGE,{"disambiguationData":[OSD([sQuery(id+"F4.wireOp",EDGE,"E10.right")])],"isStart":true})});
            var Q3;
            Q3=makeQuery(id+"F5.boolean.opBoolean","COPY",EDGE,{"derivedFrom":makeQuery(id+"F5.opExtrude","CAP_EDGE",EDGE,{"disambiguationData":[OSD([sQuery(id+"F4.wireOp",EDGE,"E10.left")])],"isStart":true})});
            var Q4;
            Q4=makeQuery(id+"F12.boolean.opBoolean","MERGE",EDGE,{"derivedFrom":[makeQuery(id+"F5.boolean.opBoolean","INTERSECT",EDGE,{"derivedFrom":[makeQuery(id+"F3.opExtrude","SWEPT_FACE",FACE,{"disambiguationData":[OSD([sQuery(id+"F2.wireOp",EDGE,"E5.top")])]}),makeQuery(id+"F5.opExtrude","SWEPT_FACE",FACE,{"disambiguationData":[OSD([sQuery(id+"F4.wireOp",EDGE,"E10.left")])]})]}),makeQuery(id+"F12.opExtrude","CAP_EDGE",EDGE,{"disambiguationData":[OSD([sQuery(id+"F11.wireOp",EDGE,"E15.right")])],"isStart":true})]});
            var Q5;
            Q5=makeQuery(id+"F5.boolean.opBoolean","COPY",EDGE,{"derivedFrom":makeQuery(id+"F5.opExtrude","CAP_EDGE",EDGE,{"disambiguationData":[OSD([sQuery(id+"F4.wireOp",EDGE,"E10.top")])],"isStart":true})});
            var Q6;
            Q6=makeQuery(id+"F5.boolean.opBoolean","INTERSECT",EDGE,{"derivedFrom":[makeQuery(id+"F3.opExtrude","SWEPT_FACE",FACE,{"disambiguationData":[OSD([sQuery(id+"F2.wireOp",EDGE,"E5.top")])]}),makeQuery(id+"F5.opExtrude","SWEPT_FACE",FACE,{"disambiguationData":[OSD([sQuery(id+"F4.wireOp",EDGE,"E10.top")])]})]});
            var Q7;
            Q7=makeQuery(id+"F5.boolean.opBoolean","COPY",EDGE,{"derivedFrom":makeQuery(id+"F5.opExtrude","CAP_EDGE",EDGE,{"disambiguationData":[OSD([sQuery(id+"F4.wireOp",EDGE,"E11.top")])],"isStart":true})});
            var Q8;
            Q8=makeQuery(id+"F5.boolean.opBoolean","INTERSECT",EDGE,{"derivedFrom":[makeQuery(id+"F3.opExtrude","SWEPT_FACE",FACE,{"disambiguationData":[OSD([sQuery(id+"F2.wireOp",EDGE,"E5.top")])]}),makeQuery(id+"F5.opExtrude","SWEPT_FACE",FACE,{"disambiguationData":[OSD([sQuery(id+"F4.wireOp",EDGE,"E11.top")])]})]});
            var Q9;
            Q9=makeQuery(id+"F12.boolean.opBoolean","MERGE",EDGE,{"derivedFrom":[makeQuery(id+"F5.boolean.opBoolean","INTERSECT",EDGE,{"derivedFrom":[makeQuery(id+"F3.opExtrude","SWEPT_FACE",FACE,{"disambiguationData":[OSD([sQuery(id+"F2.wireOp",EDGE,"E5.top")])]}),makeQuery(id+"F5.opExtrude","SWEPT_FACE",FACE,{"disambiguationData":[OSD([sQuery(id+"F4.wireOp",EDGE,"E11.right")])]})]}),makeQuery(id+"F12.opExtrude","CAP_EDGE",EDGE,{"disambiguationData":[OSD([sQuery(id+"F11.wireOp",EDGE,"E14.left")])],"isStart":true})]});
            var Q10;
            Q10=makeQuery(id+"F5.boolean.opBoolean","COPY",EDGE,{"derivedFrom":makeQuery(id+"F5.opExtrude","CAP_EDGE",EDGE,{"disambiguationData":[OSD([sQuery(id+"F4.wireOp",EDGE,"E11.right")])],"isStart":true})});
            var Q11;
            Q11=makeQuery(id+"F12.boolean.opBoolean","MERGE",EDGE,{"derivedFrom":[makeQuery(id+"F5.boolean.opBoolean","INTERSECT",EDGE,{"derivedFrom":[makeQuery(id+"F3.opExtrude","SWEPT_FACE",FACE,{"disambiguationData":[OSD([sQuery(id+"F2.wireOp",EDGE,"E5.top")])]}),makeQuery(id+"F5.opExtrude","SWEPT_FACE",FACE,{"disambiguationData":[OSD([sQuery(id+"F4.wireOp",EDGE,"E10.right")])]})]}),makeQuery(id+"F12.opExtrude","CAP_EDGE",EDGE,{"disambiguationData":[OSD([sQuery(id+"F11.wireOp",EDGE,"E15.left")])],"isStart":true})]});
            fillet(context, id + "F29", {"entities" : qUnion([Q0, Q1, Q2, Q3, Q4, Q5, Q6, Q7, Q8, Q9, Q10, Q11]), "radius" : .25 * mm, "tangentPropagation" : true, "allowEdgeOverflow" : false});
        }
        {
            var Q0;
            Q0=makeQuery(id+"F10.boolean.opBoolean","MERGE",FACE,{"derivedFrom":[makeQuery(id+"F1.opExtrude","CAP_FACE",FACE,{"disambiguationData":[OSD([sQuery(id+"F0.wireOp",EDGE,"E0.bottom"),sQuery(id+"F0.wireOp",EDGE,"E0.top"),sQuery(id+"F0.wireOp",EDGE,"E0.left"),sQuery(id+"F0.wireOp",EDGE,"E0.right"),sQuery(id+"F0.wireOp",EDGE,"E1.filletArc"),sQuery(id+"F0.wireOp",EDGE,"E2.filletArc"),sQuery(id+"F0.wireOp",EDGE,"E3.filletArc"),sQuery(id+"F0.wireOp",EDGE,"E4.filletArc")])],"isStart":false}),makeQuery(id+"F10.opExtrude","SWEPT_FACE",FACE,{"disambiguationData":[OSD([sQuery(id+"F9.wireOp",EDGE,"E13.bottom")])]})]});
            var sketch = newSketch(context, id + "F30", { "sketchPlane" : qUnion([Q0])});
            skLineSegment(sketch, "E33.bottom", {"start": v(-24, 13.4) * mm, "end": v(24, 13.4) * mm});
            skLineSegment(sketch, "E33.top", {"start": v(-20, -24.5) * mm, "end": v(20, -24.5) * mm});
            skLineSegment(sketch, "E33.left", {"start": v(-24, 13.4) * mm, "end": v(-24, -20.5) * mm});
            skLineSegment(sketch, "E33.right", {"start": v(24, 13.4) * mm, "end": v(24, -20.5) * mm});
            skPoint(sketch, "E34.visualSharp", {"position": v(-24, -24.5) * mm});
            skArc(sketch, "E34.filletArc", {"start": v(-24, -20.5) * mm, "mid": v(-22.83, -23.33) * mm, "end": v(-20, -24.5) * mm});
            skPoint(sketch, "E35.visualSharp", {"position": v(24, -24.5) * mm});
            skArc(sketch, "E35.filletArc", {"start": v(20, -24.5) * mm, "mid": v(22.83, -23.33) * mm, "end": v(24, -20.5) * mm});
            skLineSegment(sketch, "E36.bottom", {"start": v(-10, -25.5) * mm, "end": v(-16, -25.5) * mm});
            skLineSegment(sketch, "E36.top", {"start": v(-10, -24) * mm, "end": v(-16, -24) * mm});
            skLineSegment(sketch, "E36.left", {"start": v(-10, -25.5) * mm, "end": v(-10, -24) * mm});
            skLineSegment(sketch, "E36.right", {"start": v(-16, -25.5) * mm, "end": v(-16, -24) * mm});
            skLineSegment(sketch, "E37.bottom", {"start": v(-2.5, -24) * mm, "end": v(3.5, -24) * mm});
            skLineSegment(sketch, "E37.top", {"start": v(-2.5, -25.5) * mm, "end": v(3.5, -25.5) * mm});
            skLineSegment(sketch, "E37.left", {"start": v(-2.5, -24) * mm, "end": v(-2.5, -25.5) * mm});
            skLineSegment(sketch, "E37.right", {"start": v(3.5, -24) * mm, "end": v(3.5, -25.5) * mm});
            skSolve(sketch);
        }
        {
            var Q0;
            Q0 = qSketchRegion(id + "F30", true);
            extrude(context, id + "F31", {"entities" : qUnion([Q0]), "operationType" : NewBodyOperationType.REMOVE, "depth" : 40 * mm, "offsetDistance" : 25 * mm});
        }
        {
            var Q0;
            {var subQ0=sQuery(id+"F0.wireOp",EDGE,"E0.left");var subQ1=sQuery(id+"F22.wireOp",EDGE,"E28.0.3");var subQ2=sQuery(id+"F20.wireOp",EDGE,"E27.top");Q0=makeQuery(id+"F25.boolean.opBoolean","MERGE",FACE,{"derivedFrom":[makeQuery(id+"F23.boolean.opBoolean","MERGE",FACE,{"derivedFrom":[makeQuery(id+"F21.opExtrude","SWEPT_FACE",FACE,{"disambiguationData":[OSD([subQ2])]}),makeQuery(id+"F21.boolean.opBoolean","MERGE",FACE,{"derivedFrom":[makeQuery(id+"F7.boolean.opBoolean","MERGE",FACE,{"derivedFrom":[makeQuery(id+"F3.opExtrude","CAP_FACE",FACE,{"disambiguationData":[OSD([sQuery(id+"F0.wireOp",EDGE,"E0.bottom"),sQuery(id+"F0.wireOp",EDGE,"E0.top"),subQ0,sQuery(id+"F0.wireOp",EDGE,"E0.right"),sQuery(id+"F0.wireOp",EDGE,"E1.filletArc"),sQuery(id+"F0.wireOp",EDGE,"E2.filletArc"),sQuery(id+"F0.wireOp",EDGE,"E3.filletArc"),sQuery(id+"F0.wireOp",EDGE,"E4.filletArc"),sQuery(id+"F2.wireOp",EDGE,"E5.bottom"),sQuery(id+"F2.wireOp",EDGE,"E5.top"),sQuery(id+"F2.wireOp",EDGE,"E5.left"),sQuery(id+"F2.wireOp",EDGE,"E5.right"),sQuery(id+"F2.wireOp",EDGE,"E6.filletArc"),sQuery(id+"F2.wireOp",EDGE,"E7.filletArc"),sQuery(id+"F2.wireOp",EDGE,"E8.filletArc"),sQuery(id+"F2.wireOp",EDGE,"E9.filletArc")])],"isStart":false}),makeQuery(id+"F7.opExtrude","CAP_FACE",FACE,{"disambiguationData":[OSD([sQuery(id+"F6.wireOp",EDGE,"E12.bottom"),sQuery(id+"F6.wireOp",EDGE,"E12.top"),sQuery(id+"F6.wireOp",EDGE,"E12.left"),sQuery(id+"F6.wireOp",EDGE,"E12.right")])],"isStart":false})]}),makeQuery(id+"F21.opExtrude","SWEPT_FACE",FACE,{"disambiguationData":[OSD([subQ0])]})]}),makeQuery(id+"F23.opExtrude","SWEPT_FACE",FACE,{"disambiguationData":[OSD([subQ1])]})]}),makeQuery(id+"F25.opExtrude","CAP_FACE",FACE,{"disambiguationData":[OSD([subQ2,sQuery(id+"F20.wireOp",EDGE,"E27.right"),sQuery(id+"F22.wireOp",EDGE,"E28.0.2"),subQ1,sQuery(id+"F24.wireOp",EDGE,"E29"),sQuery(id+"F24.wireOp",EDGE,"E30")])],"isStart":true}),makeQuery(id+"F25.opExtrude","CAP_FACE",FACE,{"disambiguationData":[OSD([subQ0,sQuery(id+"F20.wireOp",EDGE,"E26.left"),sQuery(id+"F24.wireOp",EDGE,"E31"),sQuery(id+"F24.wireOp",EDGE,"E32")])],"isStart":true})]});}
            var sketch = newSketch(context, id + "F32", { "sketchPlane" : qUnion([Q0])});
            skLineSegment(sketch, "E38.bottom", {"start": v(26.65, 2.5) * mm, "end": v(-34.18, 2.5) * mm});
            skLineSegment(sketch, "E38.top", {"start": v(26.65, -30.15) * mm, "end": v(-34.18, -30.15) * mm});
            skLineSegment(sketch, "E38.left", {"start": v(26.65, 2.5) * mm, "end": v(26.65, -30.15) * mm});
            skLineSegment(sketch, "E38.right", {"start": v(-34.18, 2.5) * mm, "end": v(-34.18, -30.15) * mm});
            skLineSegment(sketch, "E39.bottom", {"start": v(-34.18, 2.5) * mm, "end": v(24, 2.5) * mm});
            skLineSegment(sketch, "E39.top", {"start": v(-34.18, 32.86) * mm, "end": v(24, 32.86) * mm});
            skLineSegment(sketch, "E39.left", {"start": v(-34.18, 2.5) * mm, "end": v(-34.18, 32.86) * mm});
            skLineSegment(sketch, "E39.right", {"start": v(24, 2.5) * mm, "end": v(24, 32.86) * mm});
            skSolve(sketch);
        }
        {
            var Q0;
            {var subQ5=sQuery(id+"F2.wireOp",EDGE,"E6.filletArc");var subQ28=makeQuery(id+"F3.opExtrude","CAP_EDGE",EDGE,{"disambiguationData":[OSD([subQ5])],"isStart":false});Q0=makeQuery(id+"F32.imprint","IMPRINT",FACE,{"disambiguationData":[TD([[makeQuery(id+"F32.imprint","IMPRINT",EDGE,{"derivedFrom":subQ28}),-1.0]])]});}
            var Q1;
            {var subQ6=sQuery(id+"F32.wireOp",EDGE,"E38.top");Q1=makeQuery(id+"F32.imprint","IMPRINT",FACE,{"disambiguationData":[TD([[makeQuery(id+"F32.imprint","IMPRINT",EDGE,{"derivedFrom":subQ6}),-1.0]])]});}
            var Q2;
            {var subQ1=sQuery(id+"F32.wireOp",EDGE,"E39.top");Q2=makeQuery(id+"F32.imprint","IMPRINT",FACE,{"disambiguationData":[TD([[makeQuery(id+"F32.imprint","IMPRINT",EDGE,{"derivedFrom":subQ1}),-1.0]])]});}
            var Q3;
            {var subQ2=sQuery(id+"F2.wireOp",EDGE,"E6.filletArc");var subQ3=makeQuery(id+"F3.opExtrude","CAP_EDGE",EDGE,{"disambiguationData":[OSD([subQ2])],"isStart":false});Q3=makeQuery(id+"F32.imprint","IMPRINT",FACE,{"disambiguationData":[TD([[makeQuery(id+"F32.imprint","IMPRINT",EDGE,{"derivedFrom":subQ3}),1.0]])]});}
            var Q4;
            {var subQ12=sQuery(id+"F32.wireOp",EDGE,"E38.bottom");Q4=makeQuery(id+"F32.imprint","IMPRINT",FACE,{"disambiguationData":[TD([[makeQuery(id+"F32.imprint","IMPRINT",EDGE,{"derivedFrom":subQ12}),1.0]])]});}
            var Q5;
            {var subQ1=sQuery(id+"F0.wireOp",EDGE,"E0.left");var subQ2=sQuery(id+"F22.wireOp",EDGE,"E28.0.3");var subQ3=sQuery(id+"F20.wireOp",EDGE,"E27.top");var subQ4=makeQuery(id+"F25.boolean.opBoolean","MERGE",FACE,{"derivedFrom":[makeQuery(id+"F23.boolean.opBoolean","MERGE",FACE,{"derivedFrom":[makeQuery(id+"F21.opExtrude","SWEPT_FACE",FACE,{"disambiguationData":[OSD([subQ3])]}),makeQuery(id+"F21.boolean.opBoolean","MERGE",FACE,{"derivedFrom":[makeQuery(id+"F7.boolean.opBoolean","MERGE",FACE,{"derivedFrom":[makeQuery(id+"F3.opExtrude","CAP_FACE",FACE,{"disambiguationData":[OSD([sQuery(id+"F0.wireOp",EDGE,"E0.bottom"),sQuery(id+"F0.wireOp",EDGE,"E0.top"),subQ1,sQuery(id+"F0.wireOp",EDGE,"E0.right"),sQuery(id+"F0.wireOp",EDGE,"E1.filletArc"),sQuery(id+"F0.wireOp",EDGE,"E2.filletArc"),sQuery(id+"F0.wireOp",EDGE,"E3.filletArc"),sQuery(id+"F0.wireOp",EDGE,"E4.filletArc"),sQuery(id+"F2.wireOp",EDGE,"E5.bottom"),sQuery(id+"F2.wireOp",EDGE,"E5.top"),sQuery(id+"F2.wireOp",EDGE,"E5.left"),sQuery(id+"F2.wireOp",EDGE,"E5.right"),sQuery(id+"F2.wireOp",EDGE,"E6.filletArc"),sQuery(id+"F2.wireOp",EDGE,"E7.filletArc"),sQuery(id+"F2.wireOp",EDGE,"E8.filletArc"),sQuery(id+"F2.wireOp",EDGE,"E9.filletArc")])],"isStart":false}),makeQuery(id+"F7.opExtrude","CAP_FACE",FACE,{"disambiguationData":[OSD([sQuery(id+"F6.wireOp",EDGE,"E12.bottom"),sQuery(id+"F6.wireOp",EDGE,"E12.top"),sQuery(id+"F6.wireOp",EDGE,"E12.left"),sQuery(id+"F6.wireOp",EDGE,"E12.right")])],"isStart":false})]}),makeQuery(id+"F21.opExtrude","SWEPT_FACE",FACE,{"disambiguationData":[OSD([subQ1])]})]}),makeQuery(id+"F23.opExtrude","SWEPT_FACE",FACE,{"disambiguationData":[OSD([subQ2])]})]}),makeQuery(id+"F25.opExtrude","CAP_FACE",FACE,{"disambiguationData":[OSD([subQ3,sQuery(id+"F20.wireOp",EDGE,"E27.right"),sQuery(id+"F22.wireOp",EDGE,"E28.0.2"),subQ2,sQuery(id+"F24.wireOp",EDGE,"E29"),sQuery(id+"F24.wireOp",EDGE,"E30")])],"isStart":true}),makeQuery(id+"F25.opExtrude","CAP_FACE",FACE,{"disambiguationData":[OSD([subQ1,sQuery(id+"F20.wireOp",EDGE,"E26.left"),sQuery(id+"F24.wireOp",EDGE,"E31"),sQuery(id+"F24.wireOp",EDGE,"E32")])],"isStart":true})]});Q5=makeQuery(id+"F32.imprint","IMPRINT",FACE,{"disambiguationData":[TD([[makeQuery(id+"F32.imprint","IMPRINT",EDGE,{"derivedFrom":makeQuery(id+"F31.boolean.opBoolean","INTERSECT",EDGE,{"derivedFrom":[subQ4,makeQuery(id+"F31.opExtrude","SWEPT_FACE",FACE,{"disambiguationData":[OSD([sQuery(id+"F30.wireOp",EDGE,"E37.top")])]})]})}),-1.0]])]});}
            extrude(context, id + "F33", {"entities" : qUnion([Q0, Q1, Q2, Q3, Q4, Q5]), "operationType" : NewBodyOperationType.REMOVE, "endBound" : BoundingType.THROUGH_ALL, "oppositeDirection" : true, "depth" : 25 * mm, "offsetDistance" : 25 * mm});
        }
        {
            var Q0;
            {var subQ0=sQuery(id+"F0.wireOp",EDGE,"E0.left");var subQ1=sQuery(id+"F22.wireOp",EDGE,"E28.0.3");var subQ2=sQuery(id+"F20.wireOp",EDGE,"E27.top");Q0=makeQuery(id+"F25.boolean.opBoolean","MERGE",FACE,{"derivedFrom":[makeQuery(id+"F23.boolean.opBoolean","MERGE",FACE,{"derivedFrom":[makeQuery(id+"F21.opExtrude","SWEPT_FACE",FACE,{"disambiguationData":[OSD([subQ2])]}),makeQuery(id+"F21.boolean.opBoolean","MERGE",FACE,{"derivedFrom":[makeQuery(id+"F7.boolean.opBoolean","MERGE",FACE,{"derivedFrom":[makeQuery(id+"F3.opExtrude","CAP_FACE",FACE,{"disambiguationData":[OSD([sQuery(id+"F0.wireOp",EDGE,"E0.bottom"),sQuery(id+"F0.wireOp",EDGE,"E0.top"),subQ0,sQuery(id+"F0.wireOp",EDGE,"E0.right"),sQuery(id+"F0.wireOp",EDGE,"E1.filletArc"),sQuery(id+"F0.wireOp",EDGE,"E2.filletArc"),sQuery(id+"F0.wireOp",EDGE,"E3.filletArc"),sQuery(id+"F0.wireOp",EDGE,"E4.filletArc"),sQuery(id+"F2.wireOp",EDGE,"E5.bottom"),sQuery(id+"F2.wireOp",EDGE,"E5.top"),sQuery(id+"F2.wireOp",EDGE,"E5.left"),sQuery(id+"F2.wireOp",EDGE,"E5.right"),sQuery(id+"F2.wireOp",EDGE,"E6.filletArc"),sQuery(id+"F2.wireOp",EDGE,"E7.filletArc"),sQuery(id+"F2.wireOp",EDGE,"E8.filletArc"),sQuery(id+"F2.wireOp",EDGE,"E9.filletArc")])],"isStart":false}),makeQuery(id+"F7.opExtrude","CAP_FACE",FACE,{"disambiguationData":[OSD([sQuery(id+"F6.wireOp",EDGE,"E12.bottom"),sQuery(id+"F6.wireOp",EDGE,"E12.top"),sQuery(id+"F6.wireOp",EDGE,"E12.left"),sQuery(id+"F6.wireOp",EDGE,"E12.right")])],"isStart":false})]}),makeQuery(id+"F21.opExtrude","SWEPT_FACE",FACE,{"disambiguationData":[OSD([subQ0])]})]}),makeQuery(id+"F23.opExtrude","SWEPT_FACE",FACE,{"disambiguationData":[OSD([subQ1])]})]}),makeQuery(id+"F25.opExtrude","CAP_FACE",FACE,{"disambiguationData":[OSD([subQ2,sQuery(id+"F20.wireOp",EDGE,"E27.right"),sQuery(id+"F22.wireOp",EDGE,"E28.0.2"),subQ1,sQuery(id+"F24.wireOp",EDGE,"E29"),sQuery(id+"F24.wireOp",EDGE,"E30")])],"isStart":true}),makeQuery(id+"F25.opExtrude","CAP_FACE",FACE,{"disambiguationData":[OSD([subQ0,sQuery(id+"F20.wireOp",EDGE,"E26.left"),sQuery(id+"F24.wireOp",EDGE,"E31"),sQuery(id+"F24.wireOp",EDGE,"E32")])],"isStart":true})]});}
            var sketch = newSketch(context, id + "F34", { "sketchPlane" : qUnion([Q0])});
            skLineSegment(sketch, "E40.bottom", {"start": v(26.65, 20.5) * mm, "end": v(24, 20.5) * mm});
            skLineSegment(sketch, "E40.top", {"start": v(26.65, 25.16) * mm, "end": v(24, 25.16) * mm});
            skLineSegment(sketch, "E40.left", {"start": v(26.65, 20.5) * mm, "end": v(26.65, 25.16) * mm});
            skLineSegment(sketch, "E40.right", {"start": v(24, 20.5) * mm, "end": v(24, 25.16) * mm});
            skSolve(sketch);
        }
        {
            var Q0;
            Q0=makeQuery(id+"F34.imprint","IMPRINT",FACE,{"disambiguationData":[TD([[makeQuery(id+"F34.imprint","IMPRINT",EDGE,{"derivedFrom":sQuery(id+"F34.wireOp",EDGE,"E40.bottom")}),-1.0]])]});
            var Q1;
            {var subQ1=sQuery(id+"F0.wireOp",EDGE,"E4.filletArc");var subQ2=makeQuery(id+"F3.opExtrude","CAP_EDGE",EDGE,{"disambiguationData":[OSD([subQ1])],"isStart":false});Q1=makeQuery(id+"F34.imprint","IMPRINT",FACE,{"disambiguationData":[TD([[makeQuery(id+"F34.imprint","IMPRINT",EDGE,{"derivedFrom":subQ2}),-1.0]])]});}
            var Q2;
            {var subQ0=sQuery(id+"F0.wireOp",EDGE,"E0.left");Q2=makeQuery(id+"F25.boolean.opBoolean","MERGE",FACE,{"derivedFrom":[makeQuery(id+"F23.boolean.opBoolean","MERGE",FACE,{"derivedFrom":[makeQuery(id+"F21.opExtrude","SWEPT_FACE",FACE,{"disambiguationData":[OSD([sQuery(id+"F20.wireOp",EDGE,"E27.bottom")])]}),makeQuery(id+"F21.boolean.opBoolean","MERGE",FACE,{"derivedFrom":[makeQuery(id+"F1.opExtrude","CAP_FACE",FACE,{"disambiguationData":[OSD([sQuery(id+"F0.wireOp",EDGE,"E0.bottom"),sQuery(id+"F0.wireOp",EDGE,"E0.top"),subQ0,sQuery(id+"F0.wireOp",EDGE,"E0.right"),sQuery(id+"F0.wireOp",EDGE,"E1.filletArc"),sQuery(id+"F0.wireOp",EDGE,"E2.filletArc"),sQuery(id+"F0.wireOp",EDGE,"E3.filletArc"),sQuery(id+"F0.wireOp",EDGE,"E4.filletArc")])],"isStart":true}),makeQuery(id+"F21.opExtrude","SWEPT_FACE",FACE,{"disambiguationData":[OSD([sQuery(id+"F20.wireOp",EDGE,"E26.bottom")])]})]}),makeQuery(id+"F23.opExtrude","SWEPT_FACE",FACE,{"disambiguationData":[OSD([sQuery(id+"F22.wireOp",EDGE,"E28.0.1")])]})]}),makeQuery(id+"F25.opExtrude","CAP_FACE",FACE,{"disambiguationData":[OSD([sQuery(id+"F20.wireOp",EDGE,"E27.top"),sQuery(id+"F20.wireOp",EDGE,"E27.right"),sQuery(id+"F22.wireOp",EDGE,"E28.0.2"),sQuery(id+"F22.wireOp",EDGE,"E28.0.3"),sQuery(id+"F24.wireOp",EDGE,"E29"),sQuery(id+"F24.wireOp",EDGE,"E30")])],"isStart":false}),makeQuery(id+"F25.opExtrude","CAP_FACE",FACE,{"disambiguationData":[OSD([subQ0,sQuery(id+"F20.wireOp",EDGE,"E26.left"),sQuery(id+"F24.wireOp",EDGE,"E31"),sQuery(id+"F24.wireOp",EDGE,"E32")])],"isStart":false})]});}
            extrude(context, id + "F35", {"entities" : qUnion([Q0, Q1]), "operationType" : NewBodyOperationType.ADD, "endBound" : BoundingType.UP_TO_SURFACE, "oppositeDirection" : true, "depth" : 25 * mm, "endBoundEntityFace" : qUnion([Q2]), "offsetDistance" : 25 * mm});
        }
        {
            var Q0;
            {var subQ0=sQuery(id+"F0.wireOp",EDGE,"E0.left");var subQ1=sQuery(id+"F0.wireOp",EDGE,"E4.filletArc");Q0=makeQuery(id+"F35.boolean.opBoolean","MERGE",EDGE,{"derivedFrom":[makeQuery(id+"F21.boolean.opBoolean","SPLIT",EDGE,{"disambiguationData":[TD([makeQuery(id+"F1.opExtrude","SWEPT_FACE",FACE,{"disambiguationData":[OSD([subQ1])]})])],"derivedFrom":makeQuery(id+"F1.opExtrude","CAP_EDGE",EDGE,{"disambiguationData":[OSD([subQ0])],"isStart":true})}),makeQuery(id+"F35.opExtrude","CAP_EDGE",EDGE,{"disambiguationData":[OSD([sQuery(id+"F34.wireOp",EDGE,"E40.left")])],"isStart":false})]});}
            var Q1;
            Q1=makeQuery(id+"F23.boolean.opBoolean","MERGE",EDGE,{"derivedFrom":[makeQuery(id+"F21.opExtrude","SWEPT_EDGE",EDGE,{"disambiguationData":[OSD([sQuery(id+"F20.wireOp",EDGE,"E27.bottom"),sQuery(id+"F20.wireOp",EDGE,"E27.right")])]}),makeQuery(id+"F23.opExtrude","SWEPT_EDGE",EDGE,{"disambiguationData":[OSD([sQuery(id+"F22.wireOp",EDGE,"E28.0.1"),sQuery(id+"F22.wireOp",EDGE,"E28.0.2")])]})]});
            var Q2;
            Q2=makeQuery(id+"F21.opExtrude","SWEPT_EDGE",EDGE,{"disambiguationData":[OSD([sQuery(id+"F0.wireOp",EDGE,"E0.left"),sQuery(id+"F20.wireOp",EDGE,"E26.bottom"),sQuery(id+"F20.wireOp",EDGE,"E26.left")])]});
            var Q3;
            {var subQ0=sQuery(id+"F0.wireOp",EDGE,"E0.left");Q3=makeQuery(id+"F33.boolean.opBoolean","INTERSECT",EDGE,{"derivedFrom":[makeQuery(id+"F25.boolean.opBoolean","MERGE",FACE,{"derivedFrom":[makeQuery(id+"F23.boolean.opBoolean","MERGE",FACE,{"derivedFrom":[makeQuery(id+"F21.opExtrude","SWEPT_FACE",FACE,{"disambiguationData":[OSD([sQuery(id+"F20.wireOp",EDGE,"E27.bottom")])]}),makeQuery(id+"F21.boolean.opBoolean","MERGE",FACE,{"derivedFrom":[makeQuery(id+"F1.opExtrude","CAP_FACE",FACE,{"disambiguationData":[OSD([sQuery(id+"F0.wireOp",EDGE,"E0.bottom"),sQuery(id+"F0.wireOp",EDGE,"E0.top"),subQ0,sQuery(id+"F0.wireOp",EDGE,"E0.right"),sQuery(id+"F0.wireOp",EDGE,"E1.filletArc"),sQuery(id+"F0.wireOp",EDGE,"E2.filletArc"),sQuery(id+"F0.wireOp",EDGE,"E3.filletArc"),sQuery(id+"F0.wireOp",EDGE,"E4.filletArc")])],"isStart":true}),makeQuery(id+"F21.opExtrude","SWEPT_FACE",FACE,{"disambiguationData":[OSD([sQuery(id+"F20.wireOp",EDGE,"E26.bottom")])]})]}),makeQuery(id+"F23.opExtrude","SWEPT_FACE",FACE,{"disambiguationData":[OSD([sQuery(id+"F22.wireOp",EDGE,"E28.0.1")])]})]}),makeQuery(id+"F25.opExtrude","CAP_FACE",FACE,{"disambiguationData":[OSD([sQuery(id+"F20.wireOp",EDGE,"E27.top"),sQuery(id+"F20.wireOp",EDGE,"E27.right"),sQuery(id+"F22.wireOp",EDGE,"E28.0.2"),sQuery(id+"F22.wireOp",EDGE,"E28.0.3"),sQuery(id+"F24.wireOp",EDGE,"E29"),sQuery(id+"F24.wireOp",EDGE,"E30")])],"isStart":false}),makeQuery(id+"F25.opExtrude","CAP_FACE",FACE,{"disambiguationData":[OSD([subQ0,sQuery(id+"F20.wireOp",EDGE,"E26.left"),sQuery(id+"F24.wireOp",EDGE,"E31"),sQuery(id+"F24.wireOp",EDGE,"E32")])],"isStart":false})]}),makeQuery(id+"F33.opExtrude","SWEPT_FACE",FACE,{"disambiguationData":[OSD([sQuery(id+"F32.wireOp",EDGE,"E38.bottom")])]})]});}
            var Q4;
            {var subQ0=sQuery(id+"F0.wireOp",EDGE,"E0.left");Q4=makeQuery(id+"F33.boolean.opBoolean","INTERSECT",EDGE,{"derivedFrom":[makeQuery(id+"F25.boolean.opBoolean","MERGE",FACE,{"derivedFrom":[makeQuery(id+"F23.boolean.opBoolean","MERGE",FACE,{"derivedFrom":[makeQuery(id+"F21.opExtrude","SWEPT_FACE",FACE,{"disambiguationData":[OSD([sQuery(id+"F20.wireOp",EDGE,"E27.bottom")])]}),makeQuery(id+"F21.boolean.opBoolean","MERGE",FACE,{"derivedFrom":[makeQuery(id+"F1.opExtrude","CAP_FACE",FACE,{"disambiguationData":[OSD([sQuery(id+"F0.wireOp",EDGE,"E0.bottom"),sQuery(id+"F0.wireOp",EDGE,"E0.top"),subQ0,sQuery(id+"F0.wireOp",EDGE,"E0.right"),sQuery(id+"F0.wireOp",EDGE,"E1.filletArc"),sQuery(id+"F0.wireOp",EDGE,"E2.filletArc"),sQuery(id+"F0.wireOp",EDGE,"E3.filletArc"),sQuery(id+"F0.wireOp",EDGE,"E4.filletArc")])],"isStart":true}),makeQuery(id+"F21.opExtrude","SWEPT_FACE",FACE,{"disambiguationData":[OSD([sQuery(id+"F20.wireOp",EDGE,"E26.bottom")])]})]}),makeQuery(id+"F23.opExtrude","SWEPT_FACE",FACE,{"disambiguationData":[OSD([sQuery(id+"F22.wireOp",EDGE,"E28.0.1")])]})]}),makeQuery(id+"F25.opExtrude","CAP_FACE",FACE,{"disambiguationData":[OSD([sQuery(id+"F20.wireOp",EDGE,"E27.top"),sQuery(id+"F20.wireOp",EDGE,"E27.right"),sQuery(id+"F22.wireOp",EDGE,"E28.0.2"),sQuery(id+"F22.wireOp",EDGE,"E28.0.3"),sQuery(id+"F24.wireOp",EDGE,"E29"),sQuery(id+"F24.wireOp",EDGE,"E30")])],"isStart":false}),makeQuery(id+"F25.opExtrude","CAP_FACE",FACE,{"disambiguationData":[OSD([subQ0,sQuery(id+"F20.wireOp",EDGE,"E26.left"),sQuery(id+"F24.wireOp",EDGE,"E31"),sQuery(id+"F24.wireOp",EDGE,"E32")])],"isStart":false})]}),makeQuery(id+"F33.opExtrude","SWEPT_FACE",FACE,{"disambiguationData":[OSD([sQuery(id+"F32.wireOp",EDGE,"E39.right")])]})]});}
            fillet(context, id + "F36", {"entities" : qUnion([Q0, Q1, Q2, Q3, Q4]), "tangentPropagation" : true, "radius" : .25 * mm, "defaultsChanged" : false, "vertexSettings" : [], "allowEdgeOverflow" : false});
        }
    });
